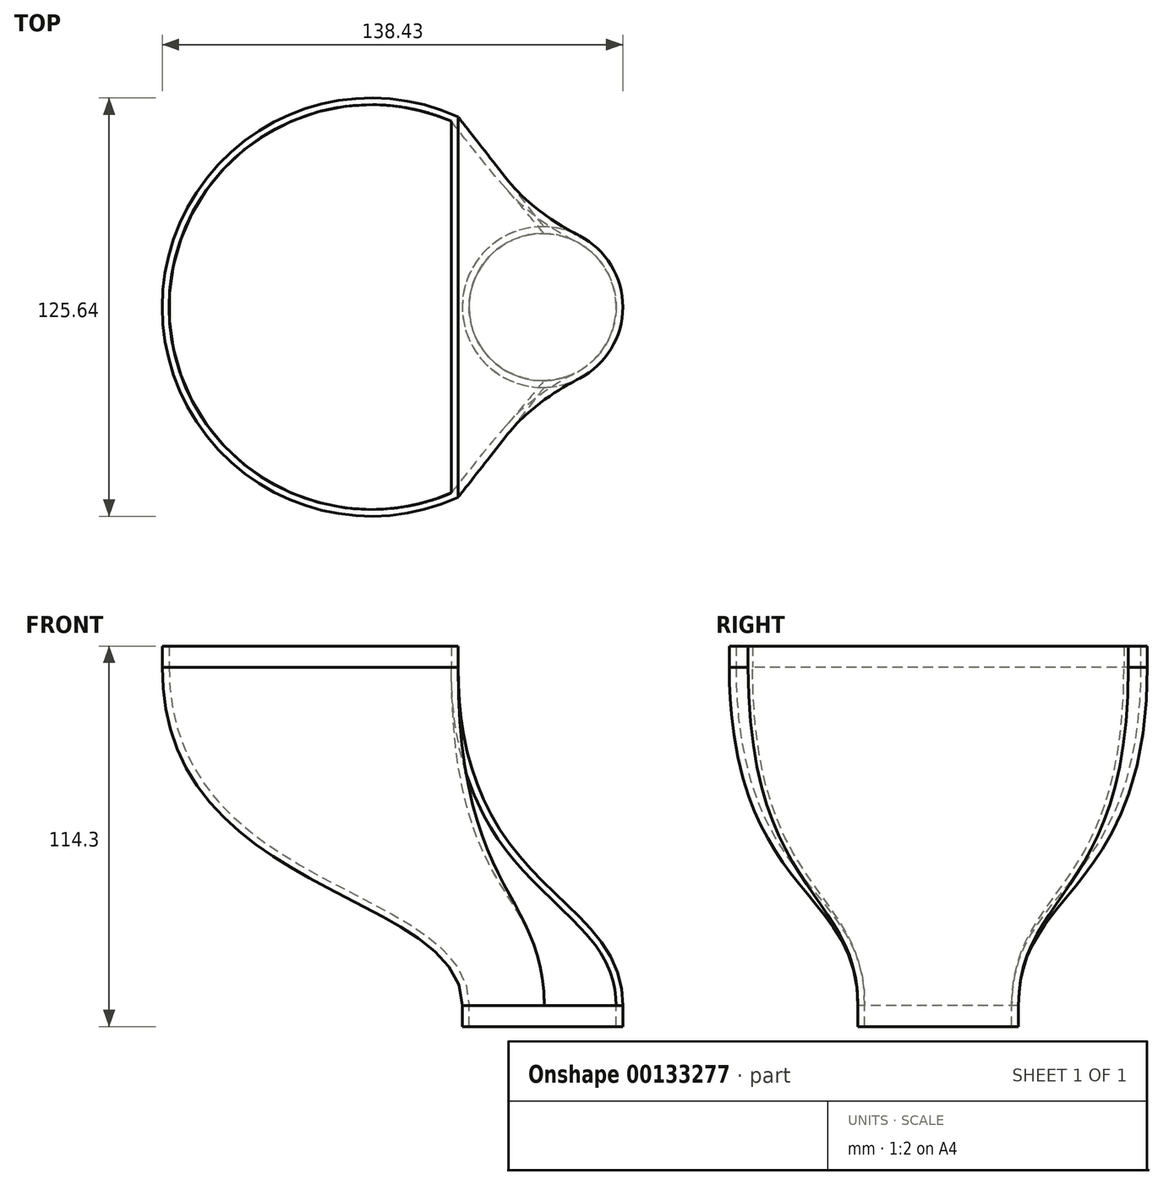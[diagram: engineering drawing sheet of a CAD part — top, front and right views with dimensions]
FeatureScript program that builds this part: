
annotation { "Feature Type Name" : "Feature", "Feature Type Description" : "" }
export const myFeature = defineFeature(function(context is Context, id is Id, definition is map)
    precondition{}
    {
        {
            var Q0;
            Q0=qCreatedBy(makeId("Top.planeOp"),FACE);
            var sketch = newSketch(context, id + "F0", { "sketchPlane" : qUnion([Q0])});
            skArc(sketch, "E0", {"start": v(0.44, 24.13) * mm, "mid": v(-24.13, -0.03) * mm, "end": v(0.5, -24.12) * mm});
            skArc(sketch, "E1", {"start": v(0.5, -24.12) * mm, "mid": v(24.13, 0.03) * mm, "end": v(0.44, 24.13) * mm});
            skSolve(sketch);
        }
        {
            var Q0;
            Q0=qCreatedBy(makeId("Top.planeOp"),FACE);
            cPlane(context, id + "F1", {"entities" : qUnion([Q0]), "cplaneType" : CPlaneType.OFFSET, "offset" : 101.6 * mm, "width" : 152.4 * mm, "height" : 152.4 * mm});
        }
        {
            var Q0;
            Q0=qCreatedBy(id+"F1.planeOp",FACE);
            var sketch = newSketch(context, id + "F2", { "sketchPlane" : qUnion([Q0])});
            skLineSegment(sketch, "E2", {"start": v(-25.4, 57.15) * mm, "end": v(-25.4, -57.15) * mm});
            skArc(sketch, "E3", {"start": v(-25.4, 57.15) * mm, "mid": v(-114.3, 0) * mm, "end": v(-25.4, -57.15) * mm});
            skPoint(sketch, "E4", {"position": v(-25.4, 0) * mm});
            skSolve(sketch);
        }
        {
            var Q0;
            Q0=makeQuery(id+"F0.imprint","IMPRINT",FACE,{"disambiguationData":[TD([[makeQuery(id+"F0.imprint","IMPRINT",EDGE,{"derivedFrom":sQuery(id+"F0.wireOp",EDGE,"E0")}),1.0]])]});
            var Q1;
            Q1=makeQuery(id+"F2.imprint","IMPRINT",FACE,{"disambiguationData":[TD([[makeQuery(id+"F2.imprint","IMPRINT",EDGE,{"derivedFrom":sQuery(id+"F2.wireOp",EDGE,"E2")}),-1.0]])]});
            loft(context, id + "F3", {"startCondition" : LoftEndDerivativeType.NORMAL_TO_PROFILE, "startMagnitude" : 1, "endCondition" : LoftEndDerivativeType.NORMAL_TO_PROFILE, "endMagnitude" : 2, "sheetProfilesArray" : [{ "sheetProfileEntities" : qUnion([Q0]) }, { "sheetProfileEntities" : qUnion([Q1]) }]});
        }
        {
            var Q0;
            Q0 = qSketchRegion(id + "F0", true);
            extrude(context, id + "F4", {"entities" : qUnion([Q0]), "operationType" : NewBodyOperationType.ADD, "oppositeDirection" : true, "depth" : 6.35 * mm});
        }
        {
            var Q0;
            Q0 = qSketchRegion(id + "F2", true);
            extrude(context, id + "F5", {"entities" : qUnion([Q0]), "operationType" : NewBodyOperationType.ADD, "depth" : 6.35 * mm});
        }
        {
            var Q0;
            Q0=makeQuery(id+"F5.opExtrude","CAP_FACE",FACE,{"disambiguationData":[OSD([sQuery(id+"F2.wireOp",EDGE,"E2"),sQuery(id+"F2.wireOp",EDGE,"E3")])],"isStart":false});
            var Q1;
            Q1=makeQuery(id+"F4.opExtrude","CAP_FACE",FACE,{"disambiguationData":[OSD([sQuery(id+"F0.wireOp",EDGE,"E0"),sQuery(id+"F0.wireOp",EDGE,"E1")])],"isStart":false});
            shell(context, id + "F6", {"entities" : qUnion([Q0, Q1]), "thickness" : 2.03 * mm});
        }
        {
            var Q0;
            Q0=qCreatedBy(makeId("Right.planeOp"),FACE);
            cPlane(context, id + "F7", {"entities" : qUnion([Q0]), "cplaneType" : CPlaneType.OFFSET, "offset" : 127 * mm, "oppositeDirection" : true, "width" : 152.4 * mm, "height" : 152.4 * mm});
        }
    });
